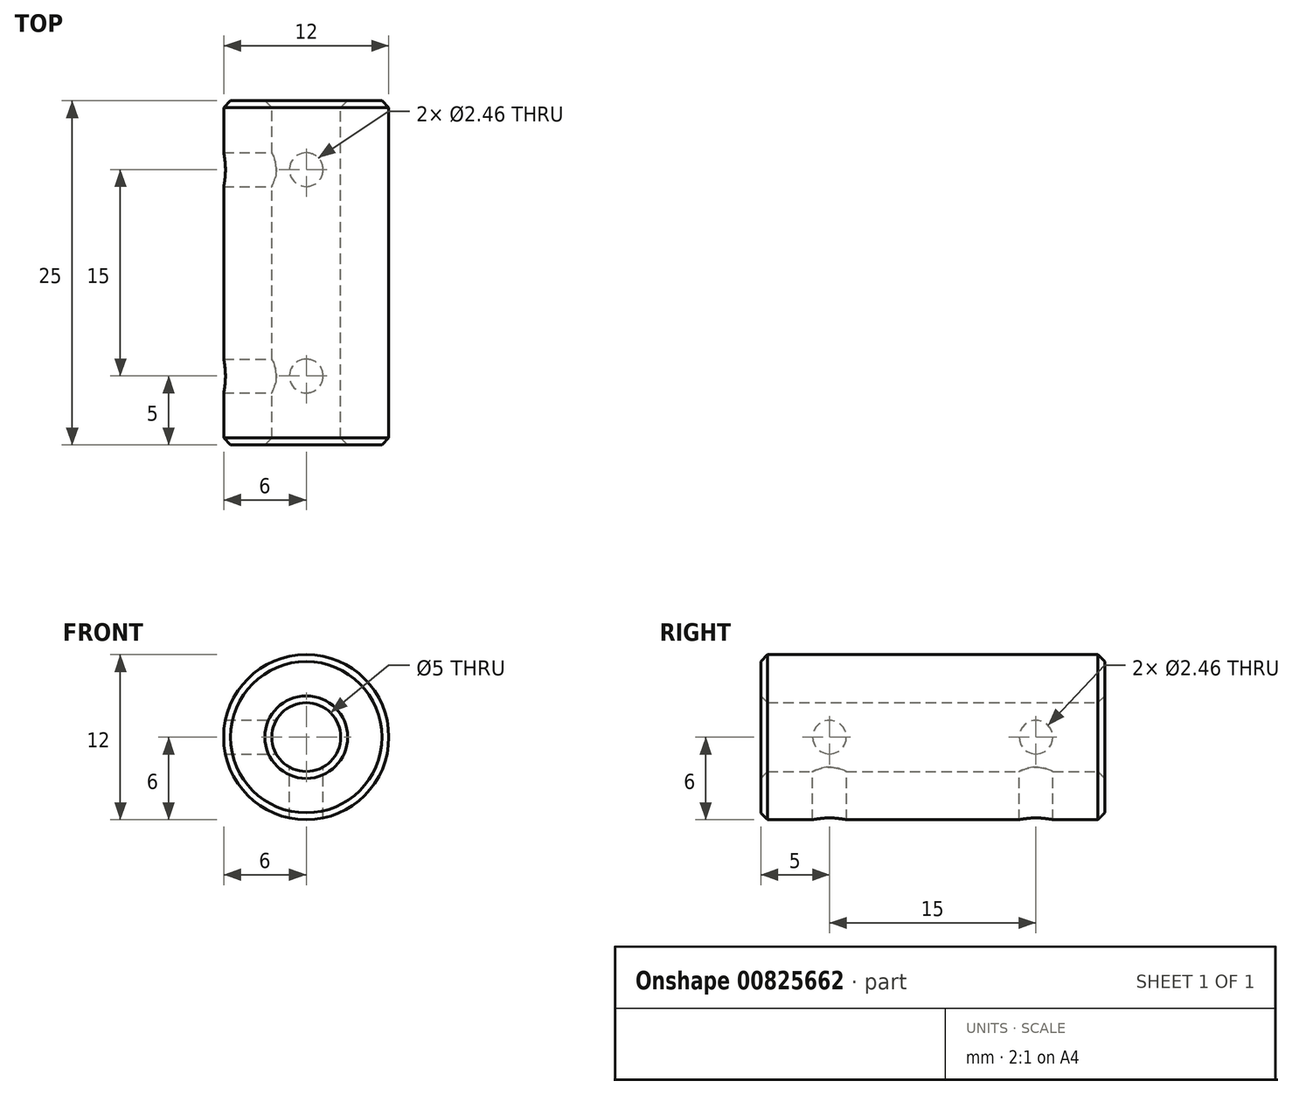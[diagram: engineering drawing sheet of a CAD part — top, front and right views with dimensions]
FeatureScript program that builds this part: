
annotation { "Feature Type Name" : "Feature", "Feature Type Description" : "" }
export const myFeature = defineFeature(function(context is Context, id is Id, definition is map)
    precondition{}
    {
        {
            var Q0;
            Q0=qCreatedBy(makeId("Front.planeOp"),FACE);
            var sketch = newSketch(context, id + "F0", { "sketchPlane" : qUnion([Q0])});
            skCircle(sketch, "E0", {"center": v(0, 0) * mm, "radius": 2.5 * mm});
            skCircle(sketch, "E1", {"center": v(0, 0) * mm, "radius": 6 * mm});
            skSolve(sketch);
        }
        {
            var Q0;
            Q0=qSketchRegion(id+"F0",true);
            extrude(context, id + "F1", {"entities" : qUnion([Q0]), "depth" : 25 * mm});
        }
        {
            var Q0;
            Q0=qCreatedBy(makeId("Top.planeOp"),FACE);
            var sketch = newSketch(context, id + "F2", { "sketchPlane" : qUnion([Q0])});
            skCircle(sketch, "E2", {"center": v(0, -5) * mm, "radius": 1.23 * mm});
            skCircle(sketch, "E3", {"center": v(0, -20) * mm, "radius": 1.23 * mm});
            skSolve(sketch);
        }
        {
            var Q0;
            Q0=qSketchRegion(id+"F2",true);
            extrude(context, id + "F3", {"entities" : qUnion([Q0]), "operationType" : NewBodyOperationType.REMOVE, "oppositeDirection" : true, "depth" : 25 * mm});
        }
        {
            var Q0;
            Q0=qCreatedBy(makeId("Right.planeOp"),FACE);
            var sketch = newSketch(context, id + "F4", { "sketchPlane" : qUnion([Q0])});
            skCircle(sketch, "E4", {"center": v(-5, 0) * mm, "radius": 1.23 * mm});
            skCircle(sketch, "E5", {"center": v(-20, 0) * mm, "radius": 1.23 * mm});
            skSolve(sketch);
        }
        {
            var Q0;
            Q0=qSketchRegion(id+"F4",true);
            extrude(context, id + "F5", {"entities" : qUnion([Q0]), "operationType" : NewBodyOperationType.REMOVE, "oppositeDirection" : true, "depth" : 25 * mm});
        }
        {
            var Q0;
            Q0=makeQuery(id+"F1.opExtrude","CAP_FACE",FACE,{"disambiguationData":[OSD([sQuery(id+"F0.wireOp",EDGE,"E0"),sQuery(id+"F0.wireOp",EDGE,"E1")])],"isStart":false});
            var Q1;
            Q1=makeQuery(id+"F1.opExtrude","CAP_FACE",FACE,{"disambiguationData":[OSD([sQuery(id+"F0.wireOp",EDGE,"E0"),sQuery(id+"F0.wireOp",EDGE,"E1")])],"isStart":true});
            chamfer(context, id + "F6", {"entities" : qUnion([Q0, Q1]), "width" : 0.5 * mm, "tangentPropagation" : true});
        }
    });
